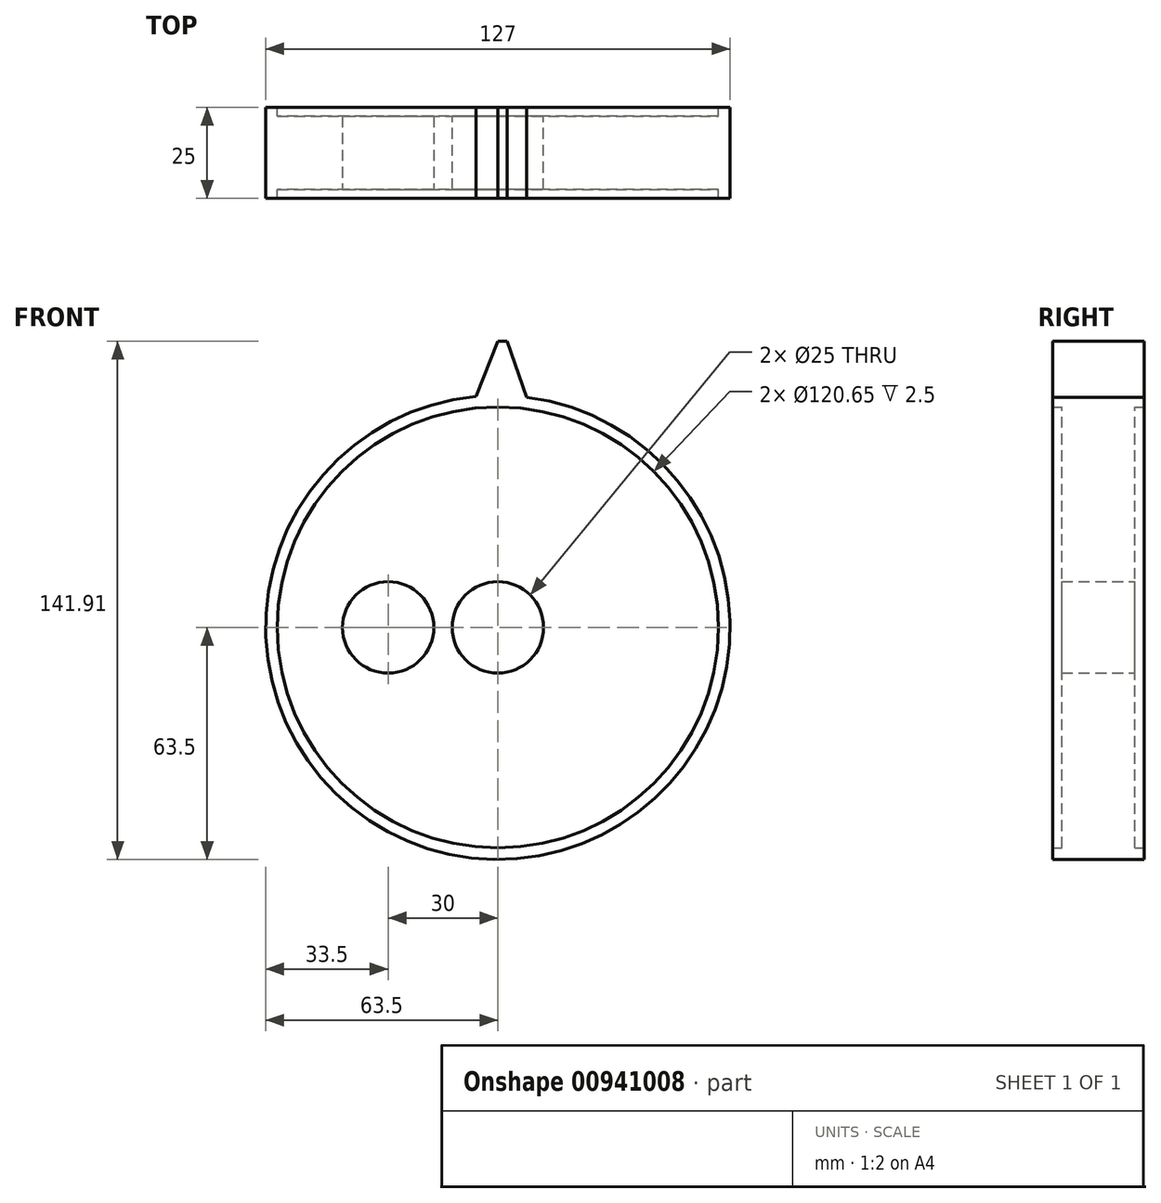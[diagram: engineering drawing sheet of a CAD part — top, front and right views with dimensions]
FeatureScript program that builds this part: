
annotation { "Feature Type Name" : "Feature", "Feature Type Description" : "" }
export const myFeature = defineFeature(function(context is Context, id is Id, definition is map)
    precondition{}
    {
        {
            var Q0;
            Q0=qCreatedBy(makeId("Front.planeOp"),FACE);
            var sketch = newSketch(context, id + "F0", { "sketchPlane" : qUnion([Q0])});
            skCircle(sketch, "E0", {"center": v(0, 0) * mm, "radius": 63.5 * mm});
            skCircle(sketch, "E1", {"center": v(0, 0) * mm, "radius": 60.33 * mm});
            skLineSegment(sketch, "E2", {"start": v(-5.97, 63.22) * mm, "end": v(0, 78.4) * mm});
            skLineSegment(sketch, "E3", {"start": v(0, 78.4) * mm, "end": v(2.54, 78.4) * mm});
            skLineSegment(sketch, "E4", {"start": v(2.54, 78.4) * mm, "end": v(7.93, 63) * mm});
            skCircle(sketch, "E5", {"center": v(0, 0) * mm, "radius": 12.5 * mm});
            skSolve(sketch);
        }
        {
            var Q0;
            Q0=makeQuery(id+"F0.imprint","IMPRINT",FACE,{"disambiguationData":[TD([[makeQuery(id+"F0.imprint","IMPRINT",EDGE,{"derivedFrom":sQuery(id+"F0.wireOp",EDGE,"E1")}),1.0]])]});
            var Q1;
            Q1=makeQuery(id+"F0.imprint","IMPRINT",FACE,{"disambiguationData":[TD([[makeQuery(id+"F0.imprint","IMPRINT",EDGE,{"derivedFrom":sQuery(id+"F0.wireOp",EDGE,"E1")}),-1.0]])]});
            extrude(context, id + "F1", {"entities" : qUnion([Q0, Q1]), "endBound" : BoundingType.SYMMETRIC, "depth" : 20 * mm, "offsetDistance" : 25.4 * mm});
        }
        {
            var Q0;
            Q0=makeQuery(id+"F0.imprint","IMPRINT",FACE,{"disambiguationData":[TD([[makeQuery(id+"F0.imprint","IMPRINT",EDGE,{"derivedFrom":sQuery(id+"F0.wireOp",EDGE,"E1")}),-1.0]])]});
            extrude(context, id + "F2", {"entities" : qUnion([Q0]), "operationType" : NewBodyOperationType.ADD, "endBound" : BoundingType.SYMMETRIC, "depth" : 25 * mm, "offsetDistance" : 25 * mm});
        }
        {
            var Q0;
            {var subQ0=sQuery(id+"F0.wireOp",EDGE,"E2");Q0=makeQuery(id+"F0.imprint","IMPRINT",FACE,{"disambiguationData":[TD([[makeQuery(id+"F0.imprint","IMPRINT",EDGE,{"derivedFrom":subQ0}),-1.0]])]});}
            extrude(context, id + "F3", {"entities" : qUnion([Q0]), "operationType" : NewBodyOperationType.ADD, "endBound" : BoundingType.SYMMETRIC, "depth" : 25 * mm, "offsetDistance" : 25 * mm});
        }
        {
            var Q0;
            Q0=makeQuery(id+"F1.opExtrude","CAP_FACE",FACE,{"disambiguationData":[OSD([sQuery(id+"F0.wireOp",EDGE,"E0")])],"isStart":false});
            var sketch = newSketch(context, id + "F4", { "sketchPlane" : qUnion([Q0])});
            skLineSegment(sketch, "E6", {"start": v(0, 0) * mm, "end": v(0, -61.32) * mm, "construction": true});
            skLineSegment(sketch, "E7", {"start": v(0, -61.32) * mm, "end": v(0, 47.68) * mm, "construction": true});
            skCircle(sketch, "E8", {"center": v(-30, 0) * mm, "radius": 12.5 * mm});
            skSolve(sketch);
        }
        {
            var Q0;
            Q0=makeQuery(id+"F4.imprint","IMPRINT",FACE,{"disambiguationData":[TD([[makeQuery(id+"F4.imprint","IMPRINT",EDGE,{"derivedFrom":sQuery(id+"F4.wireOp",EDGE,"E8")}),1.0]])]});
            extrude(context, id + "F5", {"entities" : qUnion([Q0]), "operationType" : NewBodyOperationType.REMOVE, "endBound" : BoundingType.THROUGH_ALL, "oppositeDirection" : true, "depth" : 25 * mm, "offsetDistance" : 25 * mm});
        }
    });
